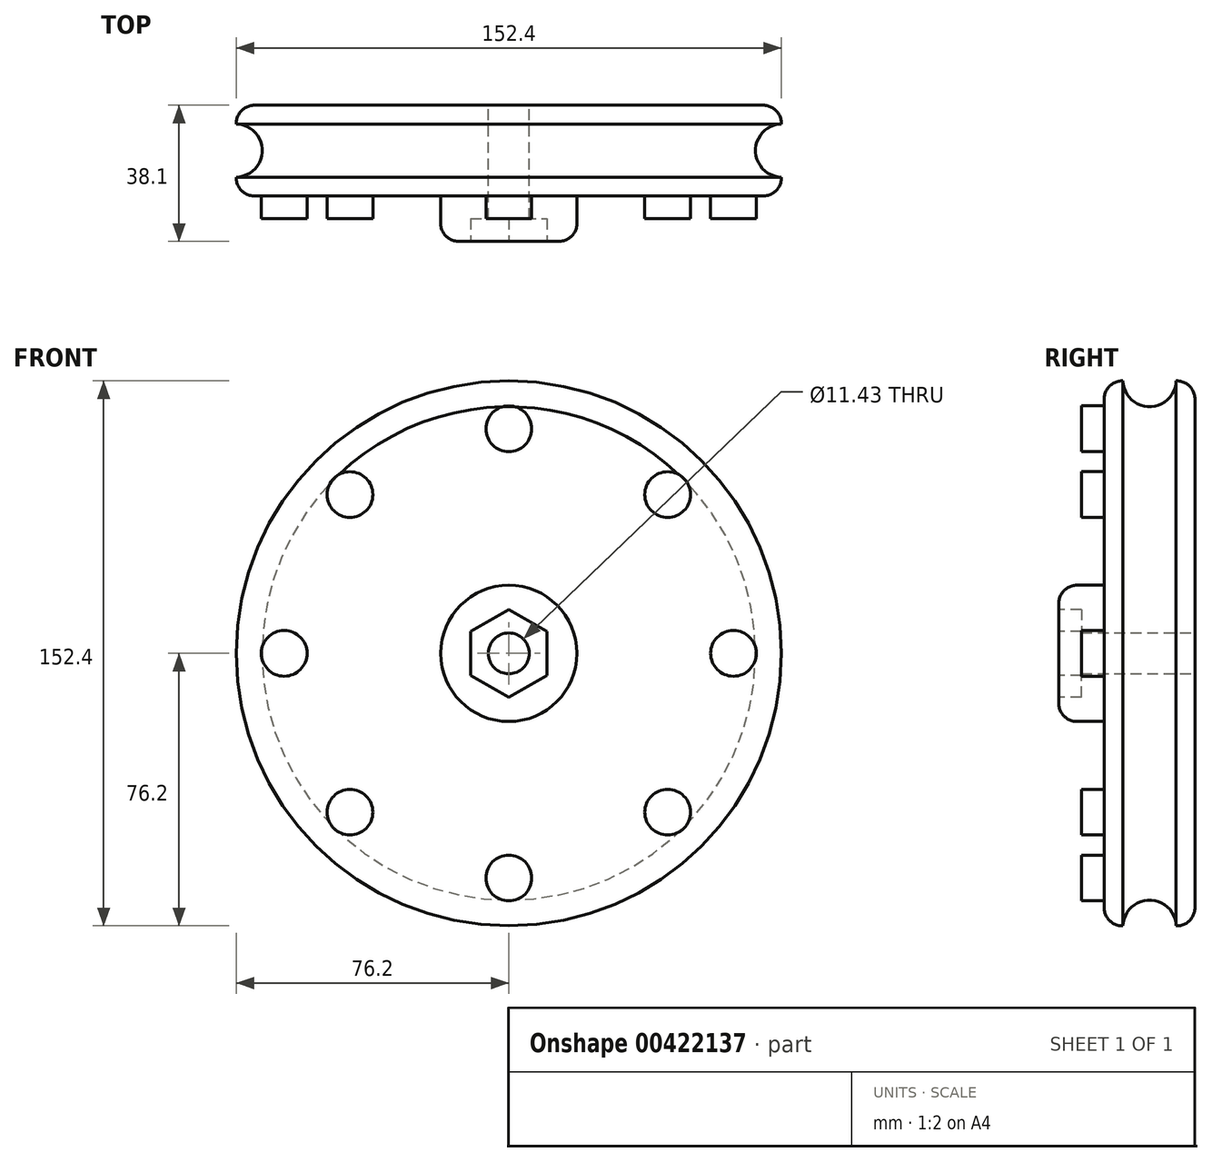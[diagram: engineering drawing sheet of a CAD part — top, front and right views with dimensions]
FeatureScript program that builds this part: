
annotation { "Feature Type Name" : "Feature", "Feature Type Description" : "" }
export const myFeature = defineFeature(function(context is Context, id is Id, definition is map)
    precondition{}
    {
        {
            var Q0;
            Q0=qCreatedBy(makeId("Front.planeOp"),FACE);
            var sketch = newSketch(context, id + "F0", { "sketchPlane" : qUnion([Q0])});
            skCircle(sketch, "E0", {"center": v(0, 0) * mm, "radius": 76.2 * mm});
            skSolve(sketch);
        }
        {
            var Q0;
            Q0=makeQuery(id+"F0.imprint","IMPRINT",FACE,{"disambiguationData":[TD([[makeQuery(id+"F0.imprint","IMPRINT",EDGE,{"derivedFrom":sQuery(id+"F0.wireOp",EDGE,"E0")}),1.0]])]});
            extrude(context, id + "F1", {"entities" : qUnion([Q0]), "depth" : 25.4 * mm});
        }
        {
            var Q0;
            Q0=makeQuery(id+"F1.opExtrude","CAP_FACE",FACE,{"disambiguationData":[OSD([sQuery(id+"F0.wireOp",EDGE,"E0")])],"isStart":false});
            var sketch = newSketch(context, id + "F2", { "sketchPlane" : qUnion([Q0])});
            skCircle(sketch, "E1", {"center": v(0, 0) * mm, "radius": 19.05 * mm});
            skSolve(sketch);
        }
        {
            var Q0;
            Q0 = qSketchRegion(id + "F2", true);
            extrude(context, id + "F3", {"entities" : qUnion([Q0]), "operationType" : NewBodyOperationType.ADD, "depth" : 12.7 * mm});
        }
        {
            var Q0;
            Q0=makeQuery(id+"F1.opExtrude","CAP_EDGE",EDGE,{"disambiguationData":[OSD([sQuery(id+"F0.wireOp",EDGE,"E0")])],"isStart":false});
            fillet(context, id + "F4", {"entities" : qUnion([Q0]), "radius" : 5.08 * mm, "tangentPropagation" : true, "allowEdgeOverflow" : false});
        }
        {
            var Q0;
            Q0=makeQuery(id+"F1.opExtrude","CAP_EDGE",EDGE,{"disambiguationData":[OSD([sQuery(id+"F0.wireOp",EDGE,"E0")])],"isStart":true});
            fillet(context, id + "F5", {"entities" : qUnion([Q0]), "radius" : 5.08 * mm, "tangentPropagation" : true, "allowEdgeOverflow" : false});
        }
        {
            var Q0;
            Q0=makeQuery(id+"F0.imprint","IMPRINT",FACE,{"disambiguationData":[TD([[makeQuery(id+"F0.imprint","IMPRINT",EDGE,{"derivedFrom":sQuery(id+"F0.wireOp",EDGE,"E0")}),1.0]])]});
            var sketch = newSketch(context, id + "F6", { "sketchPlane" : qUnion([Q0])});
            skCircle(sketch, "E2", {"center": v(0, 0) * mm, "radius": 5.72 * mm});
            skSolve(sketch);
        }
        {
            var Q0;
            Q0=makeQuery(id+"F6.imprint","IMPRINT",FACE,{"disambiguationData":[TD([[makeQuery(id+"F6.imprint","IMPRINT",EDGE,{"derivedFrom":sQuery(id+"F6.wireOp",EDGE,"E2")}),1.0]])]});
            extrude(context, id + "F7", {"entities" : qUnion([Q0]), "operationType" : NewBodyOperationType.REMOVE, "oppositeDirection" : true, "depth" : -38.1 * mm});
        }
        {
            var Q0;
            Q0=makeQuery(id+"F3.opExtrude","CAP_EDGE",EDGE,{"disambiguationData":[OSD([sQuery(id+"F2.wireOp",EDGE,"E1")])],"isStart":false});
            fillet(context, id + "F8", {"entities" : qUnion([Q0]), "radius" : 5.08 * mm, "tangentPropagation" : true, "allowEdgeOverflow" : false});
        }
        {
            var Q0;
            Q0=makeQuery(id+"F3.opExtrude","CAP_FACE",FACE,{"disambiguationData":[OSD([sQuery(id+"F2.wireOp",EDGE,"E1")])],"isStart":false});
            var sketch = newSketch(context, id + "F9", { "sketchPlane" : qUnion([Q0])});
            skCircle(sketch, "E3.cCircle", {"center": v(0, 0) * mm, "radius": 10.62 * mm, "construction": true});
            skLineSegment(sketch, "E3.0", {"start": v(10.62, 6.13) * mm, "end": v(10.62, -6.13) * mm});
            skLineSegment(sketch, "E3.1", {"start": v(10.62, -6.13) * mm, "end": v(0, -12.27) * mm});
            skLineSegment(sketch, "E3.2", {"start": v(0, -12.27) * mm, "end": v(-10.62, -6.13) * mm});
            skLineSegment(sketch, "E3.3", {"start": v(-10.62, -6.13) * mm, "end": v(-10.62, 6.13) * mm});
            skLineSegment(sketch, "E3.4", {"start": v(-10.62, 6.13) * mm, "end": v(0, 12.27) * mm});
            skLineSegment(sketch, "E3.5", {"start": v(0, 12.27) * mm, "end": v(10.62, 6.13) * mm});
            skPoint(sketch, "E3.0.midPoint", {"position": v(10.62, 0) * mm});
            skSolve(sketch);
        }
        {
            var Q0;
            Q0=makeQuery(id+"F9.imprint","IMPRINT",FACE,{"disambiguationData":[TD([[makeQuery(id+"F9.imprint","IMPRINT",EDGE,{"derivedFrom":sQuery(id+"F9.wireOp",EDGE,"E3.0")}),-1.0]])]});
            var Q1;
            Q1=sQuery(id+"F9.wireOp",EDGE,"E3.2");
            var Q2;
            Q2=sQuery(id+"F9.wireOp",EDGE,"E3.3");
            var Q3;
            Q3=sQuery(id+"F9.wireOp",EDGE,"E3.1");
            var Q4;
            Q4=sQuery(id+"F9.wireOp",EDGE,"E3.0");
            var Q5;
            Q5=sQuery(id+"F9.wireOp",EDGE,"E3.5");
            var Q6;
            Q6=sQuery(id+"F9.wireOp",EDGE,"E3.4");
            extrude(context, id + "F10", {"entities" : qUnion([Q0]), "operationType" : NewBodyOperationType.REMOVE, "surfaceEntities" : qUnion([Q1, Q2, Q3, Q4, Q5, Q6]), "oppositeDirection" : true, "depth" : 6.35 * mm});
        }
        {
            var Q0;
            Q0=qCreatedBy(makeId("Right.planeOp"),FACE);
            var sketch = newSketch(context, id + "F11", { "sketchPlane" : qUnion([Q0])});
            skCircle(sketch, "E4", {"center": v(-12.69, 76.42) * mm, "radius": 7.44 * mm});
            skPoint(sketch, "E4.first.point", {"position": v(-20.11, 75.93) * mm});
            skPoint(sketch, "E4.second.point", {"position": v(-5.25, 76.22) * mm});
            skPoint(sketch, "E4.third.point", {"position": v(-10.78, 69.23) * mm});
            skSolve(sketch);
        }
        {
            var Q0;
            Q0=makeQuery(id+"F11.imprint","IMPRINT",FACE,{"disambiguationData":[TD([[makeQuery(id+"F11.imprint","IMPRINT",EDGE,{"derivedFrom":sQuery(id+"F11.wireOp",EDGE,"E4")}),1.0]])]});
            var Q1;
            {var subQ0=sQuery(id+"F0.wireOp",EDGE,"E0");Q1=makeQuery(id+"F5.opFillet","BLEND_EDGE",EDGE,{"blendedFrom":[makeQuery(id+"F1.opExtrude","CAP_EDGE",EDGE,{"disambiguationData":[OSD([subQ0])],"isStart":true}),makeQuery(id+"F1.opExtrude","CAP_FACE",FACE,{"disambiguationData":[OSD([subQ0])],"isStart":true})],"blendedInto":[makeQuery(id+"F1.opExtrude","CAP_FACE",FACE,{"disambiguationData":[OSD([subQ0])],"isStart":true})]});}
            revolve(context, id + "F12", {"operationType" : NewBodyOperationType.REMOVE, "entities" : qUnion([Q0]), "axis" : qUnion([Q1]), "revolveType" : RevolveType.FULL, "oppositeDirection" : true});
        }
        {
            var Q0;
            Q0=makeQuery(id+"F2.imprint","IMPRINT",FACE,{"disambiguationData":[TD([[makeQuery(id+"F2.imprint","IMPRINT",EDGE,{"derivedFrom":sQuery(id+"F2.wireOp",EDGE,"E1")}),-1.0]])]});
            var sketch = newSketch(context, id + "F13", { "sketchPlane" : qUnion([Q0])});
            skCircle(sketch, "E5", {"center": v(0, 62.81) * mm, "radius": 6.4 * mm});
            skCircle(sketch, "E6.1.0", {"center": v(-44.42, 44.42) * mm, "radius": 6.4 * mm});
            skCircle(sketch, "E6.2.0", {"center": v(-62.81, 0) * mm, "radius": 6.4 * mm});
            skPoint(sketch, "E6.center", {"position": v(0, 0) * mm});
            skCircle(sketch, "E7.1.3.0", {"center": v(-44.42, -44.42) * mm, "radius": 6.4 * mm});
            skCircle(sketch, "E7.1.4.0", {"center": v(0, -62.81) * mm, "radius": 6.4 * mm});
            skCircle(sketch, "E7.1.5.0", {"center": v(44.42, -44.42) * mm, "radius": 6.4 * mm});
            skCircle(sketch, "E7.1.6.0", {"center": v(62.81, 0) * mm, "radius": 6.4 * mm});
            skCircle(sketch, "E7.1.7.0", {"center": v(44.42, 44.42) * mm, "radius": 6.4 * mm});
            skSolve(sketch);
        }
        {
            var Q0;
            Q0 = qSketchRegion(id + "F13", true);
            extrude(context, id + "F14", {"entities" : qUnion([Q0]), "operationType" : NewBodyOperationType.ADD, "depth" : 6.35 * mm, "offsetDistance" : 25.4 * mm});
        }
    });
